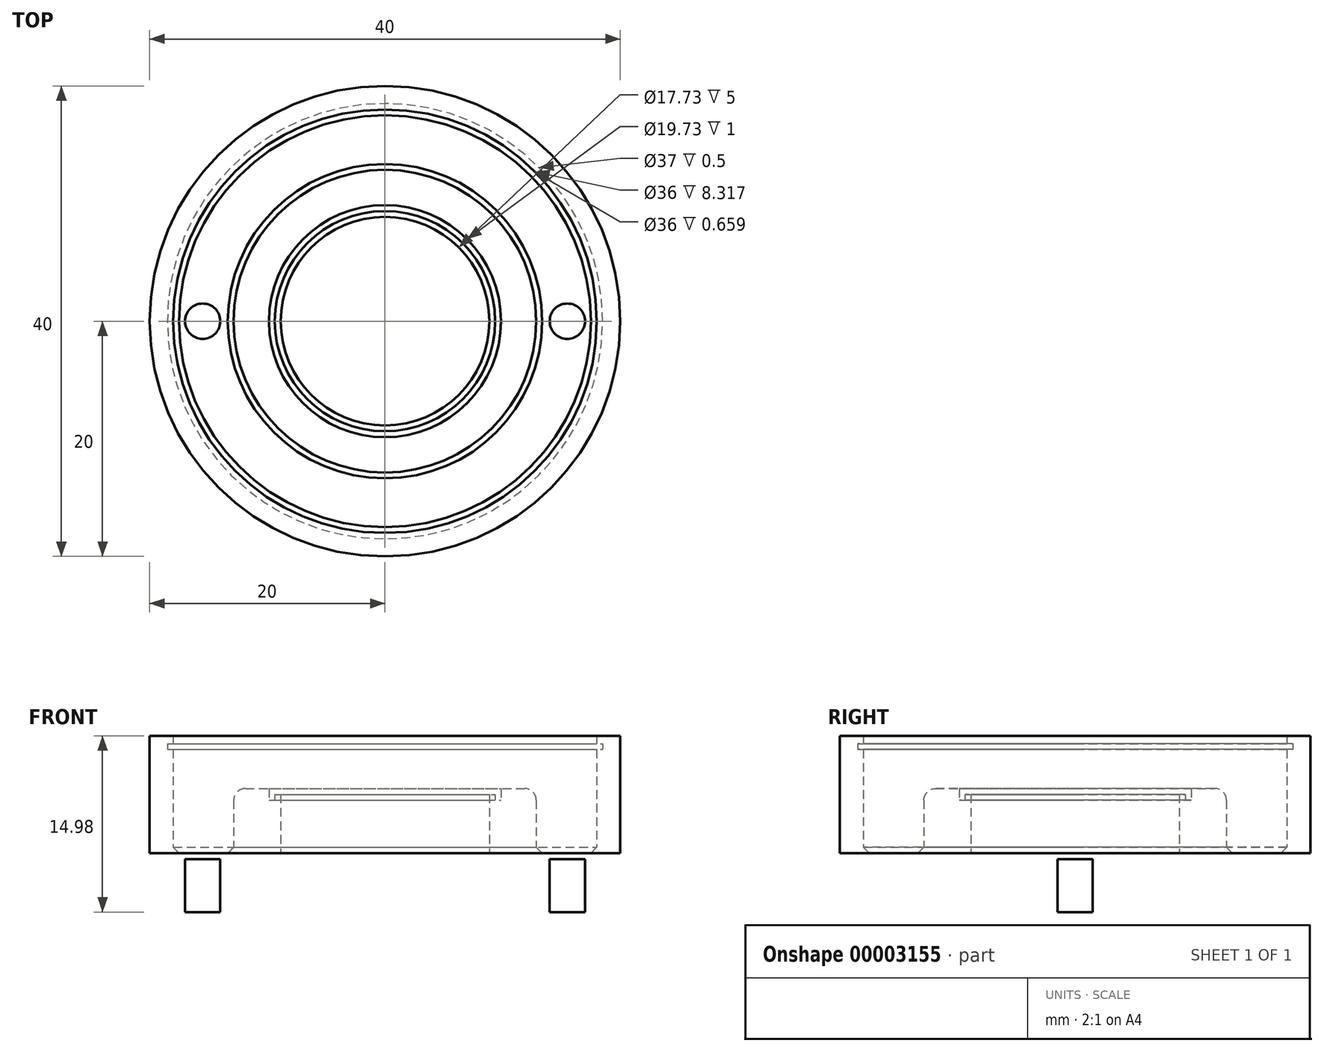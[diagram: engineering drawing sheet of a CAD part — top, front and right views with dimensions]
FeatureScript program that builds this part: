
annotation { "Feature Type Name" : "Feature", "Feature Type Description" : "" }
export const myFeature = defineFeature(function(context is Context, id is Id, definition is map)
    precondition{}
    {
        {
            var Q0;
            Q0=qCreatedBy(makeId("Front.planeOp"),FACE);
            var sketch = newSketch(context, id + "F0", { "sketchPlane" : qUnion([Q0])});
            skLineSegment(sketch, "E0", {"start": v(8.86, 0) * mm, "end": v(8.86, 10) * mm});
            skLineSegment(sketch, "E1", {"start": v(8.86, 10) * mm, "end": v(9.36, 10) * mm});
            skLineSegment(sketch, "E2", {"start": v(9.36, 10) * mm, "end": v(9.36, 9.5) * mm});
            skLineSegment(sketch, "E3", {"start": v(9.36, 9.5) * mm, "end": v(9.86, 9.5) * mm});
            skLineSegment(sketch, "E4", {"start": v(9.86, 9.5) * mm, "end": v(9.86, 10.5) * mm});
            skLineSegment(sketch, "E5", {"start": v(9.86, 10.5) * mm, "end": v(11.86, 10.5) * mm});
            skLineSegment(sketch, "E6", {"start": v(12.86, 9.5) * mm, "end": v(12.86, 4.5) * mm});
            skLineSegment(sketch, "E7", {"start": v(12.86, 4.5) * mm, "end": v(18, 4.5) * mm});
            skLineSegment(sketch, "E8", {"start": v(18, 4.5) * mm, "end": v(18, 13.82) * mm});
            skLineSegment(sketch, "E9", {"start": v(18, 13.82) * mm, "end": v(18.5, 13.82) * mm});
            skLineSegment(sketch, "E10", {"start": v(18.5, 13.82) * mm, "end": v(18.5, 14.32) * mm});
            skLineSegment(sketch, "E11", {"start": v(18.5, 14.32) * mm, "end": v(18, 14.32) * mm});
            skLineSegment(sketch, "E12", {"start": v(18, 14.32) * mm, "end": v(18, 14.98) * mm});
            skLineSegment(sketch, "E13", {"start": v(18, 14.98) * mm, "end": v(20, 14.98) * mm});
            skLineSegment(sketch, "E14", {"start": v(20, 14.98) * mm, "end": v(20, 0) * mm});
            skLineSegment(sketch, "E15", {"start": v(20, 0) * mm, "end": v(8.86, 0) * mm});
            skPoint(sketch, "E16.visualSharp", {"position": v(12.86, 10.5) * mm});
            skArc(sketch, "E16.filletArc", {"start": v(12.86, 9.5) * mm, "mid": v(12.57, 10.2) * mm, "end": v(11.86, 10.5) * mm});
            skLineSegment(sketch, "E17", {"start": v(0, 0) * mm, "end": v(0, 13.8) * mm});
            skSolve(sketch);
        }
        {
            var Q0;
            Q0=makeQuery(id+"F0.imprint","IMPRINT",FACE,{"disambiguationData":[TD([[makeQuery(id+"F0.imprint","IMPRINT",EDGE,{"derivedFrom":sQuery(id+"F0.wireOp",EDGE,"E0")}),-1.0]])]});
            var Q1;
            Q1=sQuery(id+"F0.wireOp",EDGE,"E17");
            revolve(context, id + "F1", {"entities" : qUnion([Q0]), "axis" : qUnion([Q1]), "revolveType" : RevolveType.FULL});
        }
        {
            var Q0;
            Q0=makeQuery(id+"F1.opRevolve","SWEPT_EDGE",EDGE,{"disambiguationData":[OSD([sQuery(id+"F0.wireOp",EDGE,"E7"),sQuery(id+"F0.wireOp",EDGE,"E8")])]});
            chamfer(context, id + "F2", {"entities" : qUnion([Q0]), "width" : 1 * mm, "tangentPropagation" : true});
        }
        {
            var Q0;
            Q0=makeQuery(id+"F1.opRevolve","SWEPT_EDGE",EDGE,{"disambiguationData":[OSD([sQuery(id+"F0.wireOp",EDGE,"E6"),sQuery(id+"F0.wireOp",EDGE,"E7")])]});
            chamfer(context, id + "F3", {"entities" : qUnion([Q0]), "width" : 1 * mm, "tangentPropagation" : true});
        }
        {
            var Q0;
            Q0=makeQuery(id+"F1.opRevolve","SWEPT_FACE",FACE,{"disambiguationData":[OSD([sQuery(id+"F0.wireOp",EDGE,"E15")])]});
            var sketch = newSketch(context, id + "F4", { "sketchPlane" : qUnion([Q0])});
            skCircle(sketch, "E18", {"center": v(0, 0) * mm, "radius": 15.5 * mm});
            skPoint(sketch, "E19", {"position": v(0, 15.5) * mm});
            skPoint(sketch, "E20", {"position": v(0, -15.5) * mm});
            skPoint(sketch, "E21", {"position": v(15.5, 0) * mm});
            skPoint(sketch, "E22", {"position": v(-15.5, 0) * mm});
            skCircle(sketch, "E23", {"center": v(0, 15.5) * mm, "radius": 1.5 * mm});
            skCircle(sketch, "E24", {"center": v(15.5, 0) * mm, "radius": 1.5 * mm});
            skCircle(sketch, "E25", {"center": v(0, -15.5) * mm, "radius": 1.5 * mm});
            skCircle(sketch, "E26", {"center": v(-15.5, 0) * mm, "radius": 1.5 * mm});
            skSolve(sketch);
        }
        {
            var Q0;
            {var subQ0=sQuery(id+"F4.wireOp",EDGE,"E26");var subQ1=sQuery(id+"F4.wireOp",EDGE,"E18");var subQ3=makeQuery(id+"F4.imprint","INTERSECT",VERTEX,{"disambiguationData":[OD(0.0)],"derivedFrom":[subQ1,subQ0]});Q0=makeQuery(id+"F4.imprint","IMPRINT",FACE,{"disambiguationData":[TD([[makeQuery(id+"F4.imprint","IMPRINT",EDGE,{"disambiguationData":[TD([[subQ3,-1.0]])],"derivedFrom":subQ1}),1.0]])]});}
            var Q1;
            {var subQ0=sQuery(id+"F4.wireOp",EDGE,"E26");var subQ1=sQuery(id+"F4.wireOp",EDGE,"E18");var subQ3=makeQuery(id+"F4.imprint","INTERSECT",VERTEX,{"disambiguationData":[OD(0.0)],"derivedFrom":[subQ1,subQ0]});Q1=makeQuery(id+"F4.imprint","IMPRINT",FACE,{"disambiguationData":[TD([[makeQuery(id+"F4.imprint","IMPRINT",EDGE,{"disambiguationData":[TD([[subQ3,-1.0]])],"derivedFrom":subQ1}),-1.0]])]});}
            var Q2;
            {var subQ0=sQuery(id+"F4.wireOp",EDGE,"E23");var subQ1=sQuery(id+"F4.wireOp",EDGE,"E18");var subQ3=makeQuery(id+"F4.imprint","INTERSECT",VERTEX,{"disambiguationData":[OD(0.0)],"derivedFrom":[subQ1,subQ0]});Q2=makeQuery(id+"F4.imprint","IMPRINT",FACE,{"disambiguationData":[TD([[makeQuery(id+"F4.imprint","IMPRINT",EDGE,{"disambiguationData":[TD([[subQ3,-1.0]])],"derivedFrom":subQ1}),-1.0]])]});}
            var Q3;
            {var subQ0=sQuery(id+"F4.wireOp",EDGE,"E23");var subQ1=sQuery(id+"F4.wireOp",EDGE,"E18");var subQ3=makeQuery(id+"F4.imprint","INTERSECT",VERTEX,{"disambiguationData":[OD(0.0)],"derivedFrom":[subQ1,subQ0]});Q3=makeQuery(id+"F4.imprint","IMPRINT",FACE,{"disambiguationData":[TD([[makeQuery(id+"F4.imprint","IMPRINT",EDGE,{"disambiguationData":[TD([[subQ3,-1.0]])],"derivedFrom":subQ1}),1.0]])]});}
            var Q4;
            {var subQ0=sQuery(id+"F4.wireOp",EDGE,"E24");var subQ1=sQuery(id+"F4.wireOp",EDGE,"E18");var subQ3=makeQuery(id+"F4.imprint","INTERSECT",VERTEX,{"disambiguationData":[OD(0.0)],"derivedFrom":[subQ1,subQ0]});Q4=makeQuery(id+"F4.imprint","IMPRINT",FACE,{"disambiguationData":[TD([[makeQuery(id+"F4.imprint","IMPRINT",EDGE,{"disambiguationData":[TD([[subQ3,1.0]])],"derivedFrom":subQ1}),-1.0]])]});}
            var Q5;
            {var subQ0=sQuery(id+"F4.wireOp",EDGE,"E24");var subQ1=sQuery(id+"F4.wireOp",EDGE,"E18");var subQ3=makeQuery(id+"F4.imprint","INTERSECT",VERTEX,{"disambiguationData":[OD(0.0)],"derivedFrom":[subQ1,subQ0]});Q5=makeQuery(id+"F4.imprint","IMPRINT",FACE,{"disambiguationData":[TD([[makeQuery(id+"F4.imprint","IMPRINT",EDGE,{"disambiguationData":[TD([[subQ3,1.0]])],"derivedFrom":subQ1}),1.0]])]});}
            var Q6;
            {var subQ0=sQuery(id+"F4.wireOp",EDGE,"E25");var subQ1=sQuery(id+"F4.wireOp",EDGE,"E18");var subQ3=makeQuery(id+"F4.imprint","INTERSECT",VERTEX,{"disambiguationData":[OD(0.0)],"derivedFrom":[subQ1,subQ0]});Q6=makeQuery(id+"F4.imprint","IMPRINT",FACE,{"disambiguationData":[TD([[makeQuery(id+"F4.imprint","IMPRINT",EDGE,{"disambiguationData":[TD([[subQ3,-1.0]])],"derivedFrom":subQ1}),1.0]])]});}
            var Q7;
            {var subQ0=sQuery(id+"F4.wireOp",EDGE,"E25");var subQ1=sQuery(id+"F4.wireOp",EDGE,"E18");var subQ3=makeQuery(id+"F4.imprint","INTERSECT",VERTEX,{"disambiguationData":[OD(0.0)],"derivedFrom":[subQ1,subQ0]});Q7=makeQuery(id+"F4.imprint","IMPRINT",FACE,{"disambiguationData":[TD([[makeQuery(id+"F4.imprint","IMPRINT",EDGE,{"disambiguationData":[TD([[subQ3,-1.0]])],"derivedFrom":subQ1}),-1.0]])]});}
            extrude(context, id + "F5", {"entities" : qUnion([Q0, Q1, Q2, Q3, Q4, Q5, Q6, Q7]), "operationType" : NewBodyOperationType.REMOVE, "oppositeDirection" : true, "depth" : 5 * mm});
        }
    });
